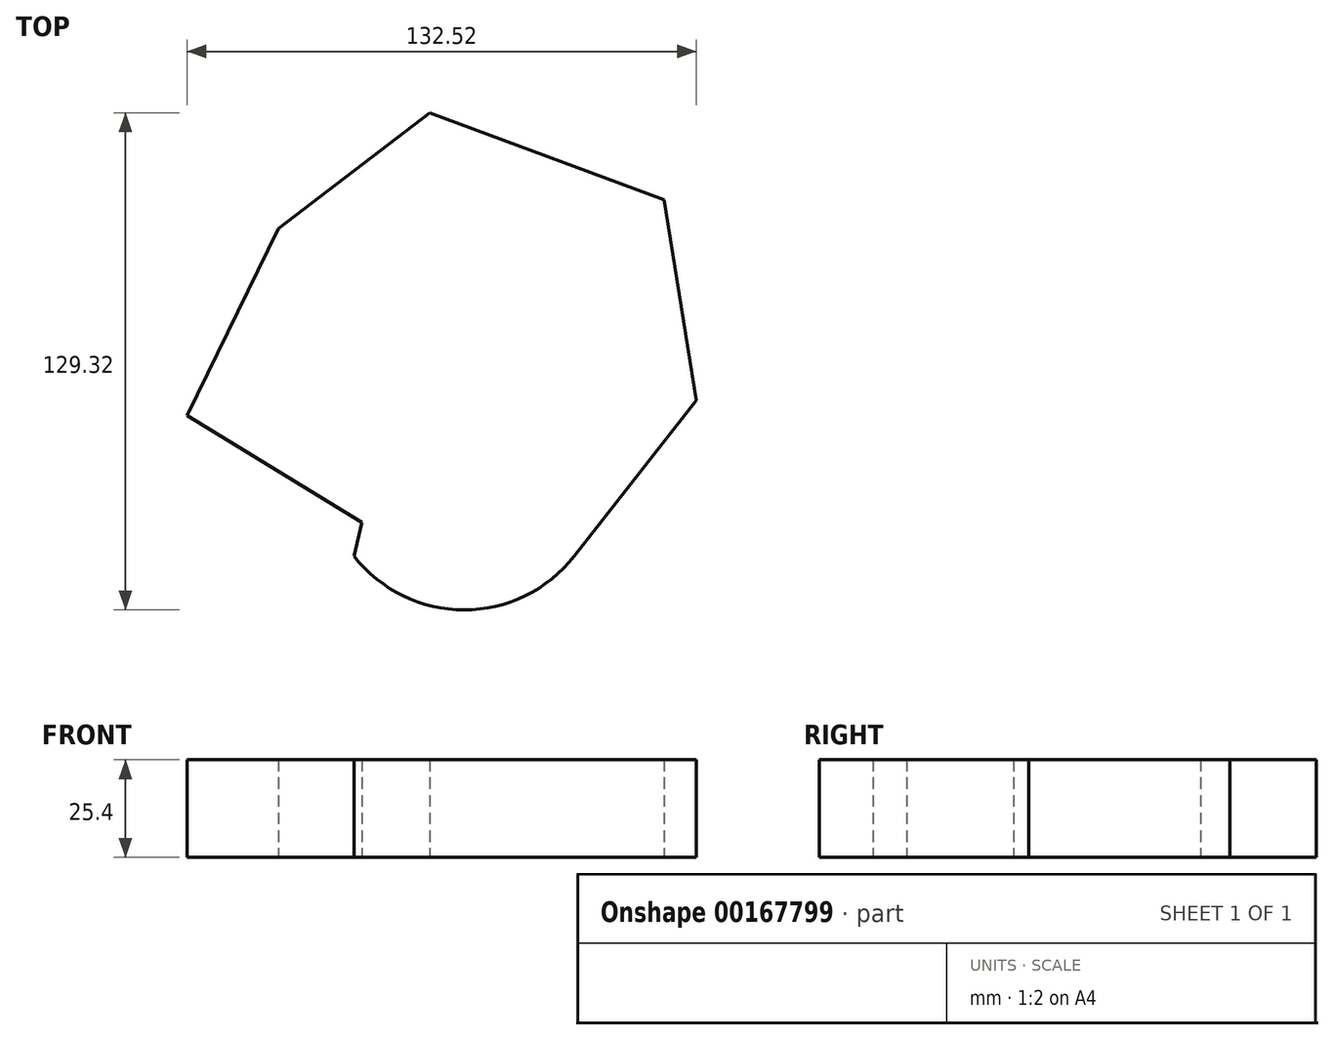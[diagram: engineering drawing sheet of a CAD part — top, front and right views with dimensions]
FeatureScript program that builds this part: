
annotation { "Feature Type Name" : "Feature", "Feature Type Description" : "" }
export const myFeature = defineFeature(function(context is Context, id is Id, definition is map)
    precondition{}
    {
        {
            var Q0;
            Q0=qCreatedBy(makeId("Top.planeOp"),FACE);
            var sketch = newSketch(context, id + "F1", { "sketchPlane" : qUnion([Q0])});
            skLineSegment(sketch, "E0", {"start": v(0, 0) * mm, "end": v(23.83, 48.7) * mm});
            skLineSegment(sketch, "E1", {"start": v(23.83, 48.7) * mm, "end": v(63.12, 78.8) * mm});
            skLineSegment(sketch, "E2", {"start": v(63.12, 78.8) * mm, "end": v(124.16, 56.23) * mm});
            skLineSegment(sketch, "E3", {"start": v(124.16, 56.23) * mm, "end": v(132.52, 3.97) * mm});
            skLineSegment(sketch, "E4", {"start": v(132.52, 3.97) * mm, "end": v(100.75, -36.58) * mm});
            skArc(sketch, "E5", {"start": v(43.48, -36.58) * mm, "mid": v(72.11, -50.52) * mm, "end": v(100.75, -36.58) * mm});
            skLineSegment(sketch, "E6", {"start": v(45.57, -27.8) * mm, "end": v(0, 0) * mm});
            skLineSegment(sketch, "E7", {"start": v(45.57, -27.8) * mm, "end": v(43.48, -36.58) * mm});
            skSolve(sketch);
        }
        {
            var Q0;
            Q0 = qSketchRegion(id + "F1", true);
            extrude(context, id + "F2", {"entities" : qUnion([Q0]), "depth" : 25.4 * mm});
        }
    });
